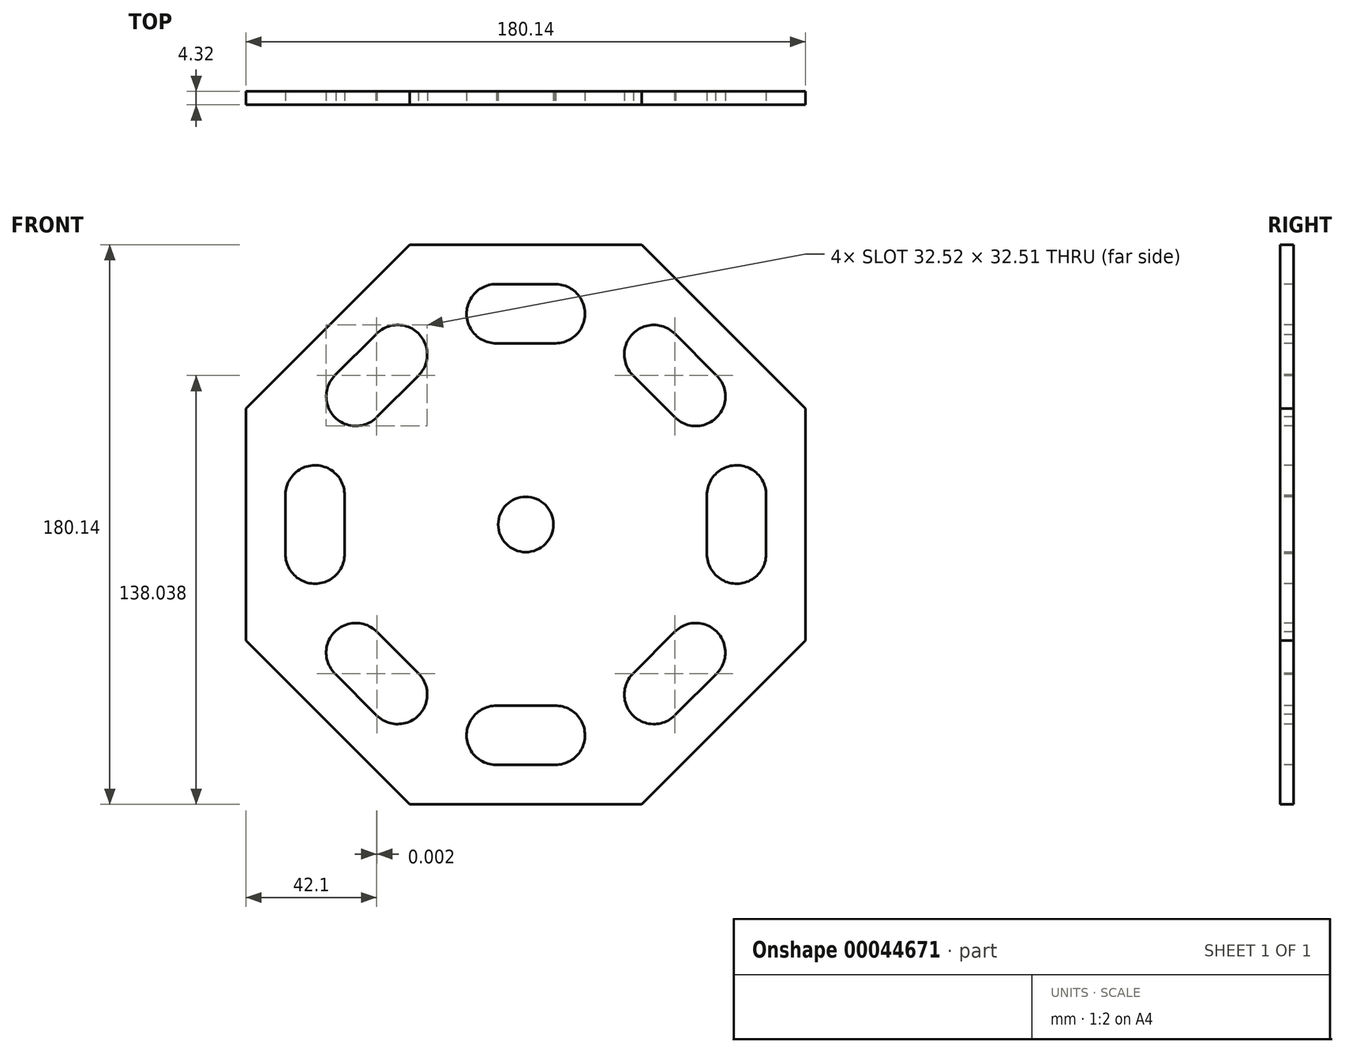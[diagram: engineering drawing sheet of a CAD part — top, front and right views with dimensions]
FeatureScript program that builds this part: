
annotation { "Feature Type Name" : "Feature", "Feature Type Description" : "" }
export const myFeature = defineFeature(function(context is Context, id is Id, definition is map)
    precondition{}
    {
        {
            var Q0;
            Q0=qCreatedBy(makeId("Front.planeOp"),FACE);
            var sketch = newSketch(context, id + "F0", { "sketchPlane" : qUnion([Q0])});
            skCircle(sketch, "E0.cCircle", {"center": v(0, 0) * mm, "radius": 90.07 * mm, "construction": true});
            skLineSegment(sketch, "E0.0", {"start": v(-90.07, 37.3) * mm, "end": v(-37.3, 90.07) * mm});
            skLineSegment(sketch, "E0.1", {"start": v(-37.3, 90.07) * mm, "end": v(37.3, 90.07) * mm});
            skLineSegment(sketch, "E0.2", {"start": v(37.3, 90.07) * mm, "end": v(90.07, 37.3) * mm});
            skLineSegment(sketch, "E0.3", {"start": v(90.07, 37.3) * mm, "end": v(90.07, -37.3) * mm});
            skLineSegment(sketch, "E0.4", {"start": v(90.07, -37.3) * mm, "end": v(37.3, -90.07) * mm});
            skLineSegment(sketch, "E0.5", {"start": v(37.3, -90.07) * mm, "end": v(-37.3, -90.07) * mm});
            skLineSegment(sketch, "E0.6", {"start": v(-37.3, -90.07) * mm, "end": v(-90.07, -37.3) * mm});
            skLineSegment(sketch, "E0.7", {"start": v(-90.07, -37.3) * mm, "end": v(-90.07, 37.3) * mm});
            skPoint(sketch, "E0.0.midPoint", {"position": v(-63.69, 63.69) * mm});
            skSolve(sketch);
        }
        {
            var Q0;
            Q0=makeQuery(id+"F0.imprint","IMPRINT",FACE,{"disambiguationData":[TD([[makeQuery(id+"F0.imprint","IMPRINT",EDGE,{"derivedFrom":sQuery(id+"F0.wireOp",EDGE,"E0.0")}),-1.0]])]});
            extrude(context, id + "F1", {"entities" : qUnion([Q0]), "depth" : 4.32 * mm});
        }
        {
            var Q0;
            Q0=makeQuery(id+"F1.opExtrude","CAP_FACE",FACE,{"disambiguationData":[OSD([sQuery(id+"F0.wireOp",EDGE,"E0.0"),sQuery(id+"F0.wireOp",EDGE,"E0.1"),sQuery(id+"F0.wireOp",EDGE,"E0.2"),sQuery(id+"F0.wireOp",EDGE,"E0.3"),sQuery(id+"F0.wireOp",EDGE,"E0.4"),sQuery(id+"F0.wireOp",EDGE,"E0.5"),sQuery(id+"F0.wireOp",EDGE,"E0.6"),sQuery(id+"F0.wireOp",EDGE,"E0.7")])],"isStart":false});
            var sketch = newSketch(context, id + "F2", { "sketchPlane" : qUnion([Q0])});
            skArc(sketch, "E1", {"start": v(-9.52, 77.37) * mm, "mid": v(-19.05, 67.77) * mm, "end": v(-9.38, 58.32) * mm});
            skArc(sketch, "E2", {"start": v(9.38, 58.32) * mm, "mid": v(19.05, 68) * mm, "end": v(9.06, 77.35) * mm});
            skLineSegment(sketch, "E3", {"start": v(9.06, 77.35) * mm, "end": v(-9.52, 77.37) * mm});
            skLineSegment(sketch, "E4", {"start": v(-9.38, 58.32) * mm, "end": v(9.67, 58.32) * mm});
            skLineSegment(sketch, "E5.1.0", {"start": v(-47.87, 34.6) * mm, "end": v(-34.4, 48.07) * mm});
            skLineSegment(sketch, "E5.1.1", {"start": v(-48.3, 61.1) * mm, "end": v(-61.44, 47.97) * mm});
            skArc(sketch, "E5.1.2", {"start": v(-61.44, 47.97) * mm, "mid": v(-61.4, 34.45) * mm, "end": v(-47.87, 34.6) * mm});
            skArc(sketch, "E5.1.3", {"start": v(-34.6, 47.87) * mm, "mid": v(-34.62, 61.55) * mm, "end": v(-48.3, 61.1) * mm});
            skLineSegment(sketch, "E5.2.0", {"start": v(-58.32, -9.38) * mm, "end": v(-58.32, 9.67) * mm});
            skLineSegment(sketch, "E5.2.1", {"start": v(-77.35, 9.06) * mm, "end": v(-77.37, -9.52) * mm});
            skArc(sketch, "E5.2.2", {"start": v(-77.37, -9.52) * mm, "mid": v(-67.77, -19.05) * mm, "end": v(-58.32, -9.38) * mm});
            skArc(sketch, "E5.2.3", {"start": v(-58.32, 9.38) * mm, "mid": v(-68, 19.05) * mm, "end": v(-77.35, 9.06) * mm});
            skLineSegment(sketch, "E5.3.0", {"start": v(-34.6, -47.87) * mm, "end": v(-48.07, -34.4) * mm});
            skLineSegment(sketch, "E5.3.1", {"start": v(-61.1, -48.3) * mm, "end": v(-47.97, -61.44) * mm});
            skArc(sketch, "E5.3.2", {"start": v(-47.97, -61.44) * mm, "mid": v(-34.45, -61.4) * mm, "end": v(-34.6, -47.87) * mm});
            skArc(sketch, "E5.3.3", {"start": v(-47.87, -34.6) * mm, "mid": v(-61.55, -34.62) * mm, "end": v(-61.1, -48.3) * mm});
            skLineSegment(sketch, "E5.4.0", {"start": v(9.38, -58.32) * mm, "end": v(-9.67, -58.32) * mm});
            skLineSegment(sketch, "E5.4.1", {"start": v(-9.06, -77.35) * mm, "end": v(9.52, -77.37) * mm});
            skArc(sketch, "E5.4.2", {"start": v(9.52, -77.37) * mm, "mid": v(19.05, -67.77) * mm, "end": v(9.38, -58.32) * mm});
            skArc(sketch, "E5.4.3", {"start": v(-9.38, -58.32) * mm, "mid": v(-19.05, -68) * mm, "end": v(-9.06, -77.35) * mm});
            skLineSegment(sketch, "E5.5.0", {"start": v(47.87, -34.6) * mm, "end": v(34.4, -48.07) * mm});
            skLineSegment(sketch, "E5.5.1", {"start": v(48.3, -61.1) * mm, "end": v(61.44, -47.97) * mm});
            skArc(sketch, "E5.5.2", {"start": v(61.44, -47.97) * mm, "mid": v(61.4, -34.45) * mm, "end": v(47.87, -34.6) * mm});
            skArc(sketch, "E5.5.3", {"start": v(34.6, -47.87) * mm, "mid": v(34.62, -61.55) * mm, "end": v(48.3, -61.1) * mm});
            skLineSegment(sketch, "E5.6.0", {"start": v(58.32, 9.38) * mm, "end": v(58.32, -9.67) * mm});
            skLineSegment(sketch, "E5.6.1", {"start": v(77.35, -9.06) * mm, "end": v(77.37, 9.52) * mm});
            skArc(sketch, "E5.6.2", {"start": v(77.37, 9.52) * mm, "mid": v(67.77, 19.05) * mm, "end": v(58.32, 9.38) * mm});
            skArc(sketch, "E5.6.3", {"start": v(58.32, -9.38) * mm, "mid": v(68, -19.05) * mm, "end": v(77.35, -9.06) * mm});
            skLineSegment(sketch, "E5.7.0", {"start": v(34.6, 47.87) * mm, "end": v(48.07, 34.4) * mm});
            skLineSegment(sketch, "E5.7.1", {"start": v(61.1, 48.3) * mm, "end": v(47.97, 61.44) * mm});
            skArc(sketch, "E5.7.2", {"start": v(47.97, 61.44) * mm, "mid": v(34.45, 61.4) * mm, "end": v(34.6, 47.87) * mm});
            skArc(sketch, "E5.7.3", {"start": v(47.87, 34.6) * mm, "mid": v(61.55, 34.62) * mm, "end": v(61.1, 48.3) * mm});
            skPoint(sketch, "E5.center", {"position": v(0, 0) * mm});
            skSolve(sketch);
        }
        {
            var Q0;
            {var subQ4=sQuery(id+"F2.wireOp",EDGE,"E1");Q0=makeQuery(id+"F2.imprint","IMPRINT",FACE,{"disambiguationData":[TD([[makeQuery(id+"F2.imprint","IMPRINT",EDGE,{"derivedFrom":subQ4}),1.0]])]});}
            extrude(context, id + "F3", {"entities" : qUnion([Q0]), "operationType" : NewBodyOperationType.REMOVE, "endBound" : BoundingType.THROUGH_ALL, "oppositeDirection" : true, "depth" : 25.4 * mm});
        }
        {
            var Q0;
            Q0=qSketchRegion(id+"F2",true);
            extrude(context, id + "F4", {"entities" : qUnion([Q0]), "operationType" : NewBodyOperationType.REMOVE, "endBound" : BoundingType.THROUGH_ALL, "oppositeDirection" : true, "depth" : 25.4 * mm});
        }
        {
            var Q0;
            Q0=makeQuery(id+"F1.opExtrude","CAP_FACE",FACE,{"disambiguationData":[OSD([sQuery(id+"F0.wireOp",EDGE,"E0.0"),sQuery(id+"F0.wireOp",EDGE,"E0.1"),sQuery(id+"F0.wireOp",EDGE,"E0.2"),sQuery(id+"F0.wireOp",EDGE,"E0.3"),sQuery(id+"F0.wireOp",EDGE,"E0.4"),sQuery(id+"F0.wireOp",EDGE,"E0.5"),sQuery(id+"F0.wireOp",EDGE,"E0.6"),sQuery(id+"F0.wireOp",EDGE,"E0.7")])],"isStart":false});
            var sketch = newSketch(context, id + "F5", { "sketchPlane" : qUnion([Q0])});
            skPoint(sketch, "E6", {"position": v(0, 0) * mm});
            skSolve(sketch);
        }
        {
            var Q0;
            Q0=sQuery(id+"F5.wireOp",VERTEX,"E6");
            var Q1;
            Q1=makeQuery(id+"F1.opExtrude","SWEPT_BODY",BODY,{"disambiguationData":[OSD([sQuery(id+"F0.wireOp",EDGE,"E0.0"),sQuery(id+"F0.wireOp",EDGE,"E0.1"),sQuery(id+"F0.wireOp",EDGE,"E0.2"),sQuery(id+"F0.wireOp",EDGE,"E0.3"),sQuery(id+"F0.wireOp",EDGE,"E0.4"),sQuery(id+"F0.wireOp",EDGE,"E0.5"),sQuery(id+"F0.wireOp",EDGE,"E0.6"),sQuery(id+"F0.wireOp",EDGE,"E0.7")])]});
            hole(context, id + "F6", {"style" : HoleStyle.SIMPLE, "holeDiameter" : 17.78 * mm, "endStyle" : HoleEndStyle.THROUGH, "locations" : qUnion([Q0]), "scope" : qUnion([Q1])});
        }
    });
